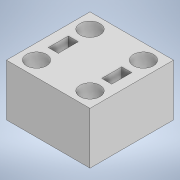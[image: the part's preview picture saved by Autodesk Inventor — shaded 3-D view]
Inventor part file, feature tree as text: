
AUTODESK INVENTOR PART (.ipt)
format: ipt  version: 2020 (Build 240168000, 168)  size: 205,824 bytes
history: native  units: mm
features: extrude x4, sketch x4
ambient origin geometry x8: Origin, YZ Plane, XZ Plane, XY Plane, X Axis, Y Axis, Z Axis, Center Point
bodies: Solid1 (feature_tree)
feature tree (8):
  extrude  "Extrusion1"  Depth=25.0mm
  extrude  "Extrusion3"  Depth=2.5mm
  extrude  "Extrusion4"  Depth=2.5mm
  extrude  "Extrusion5"  Depth=6.0mm
  sketch  "Sketch1"  dims[d0=25.0mm d1=25.0mm]
  sketch  "Sketch4"  dims[d2=2.5mm d3=2.5mm]
  sketch  "Sketch5"  dims[d4=2.5mm d5=2.5mm]
  sketch  "Sketch6"  dims[d6=2.5mm d8=6.0mm d9=6.0mm d10=6.0mm d11=6.0mm d12=5.0mm d13=0.0mm d18=24.0mm d19=24.0mm d20=0.5mm d21=0.0mm d22=3.5mm d23=6.0mm d24=3.5mm d25=3.5mm d26=6.0mm d27=3.5mm d28=6.0mm d29=6.0mm d30=6.0mm d31=6.0mm d32=5.0mm d33=0.0mm d34=1.5mm d35=1.5mm d36=1.5mm d37=1.5mm d38=6.0mm d39=6.0mm d40=6.0mm d41=6.0mm d42=5.0mm d43=0.0mm]
